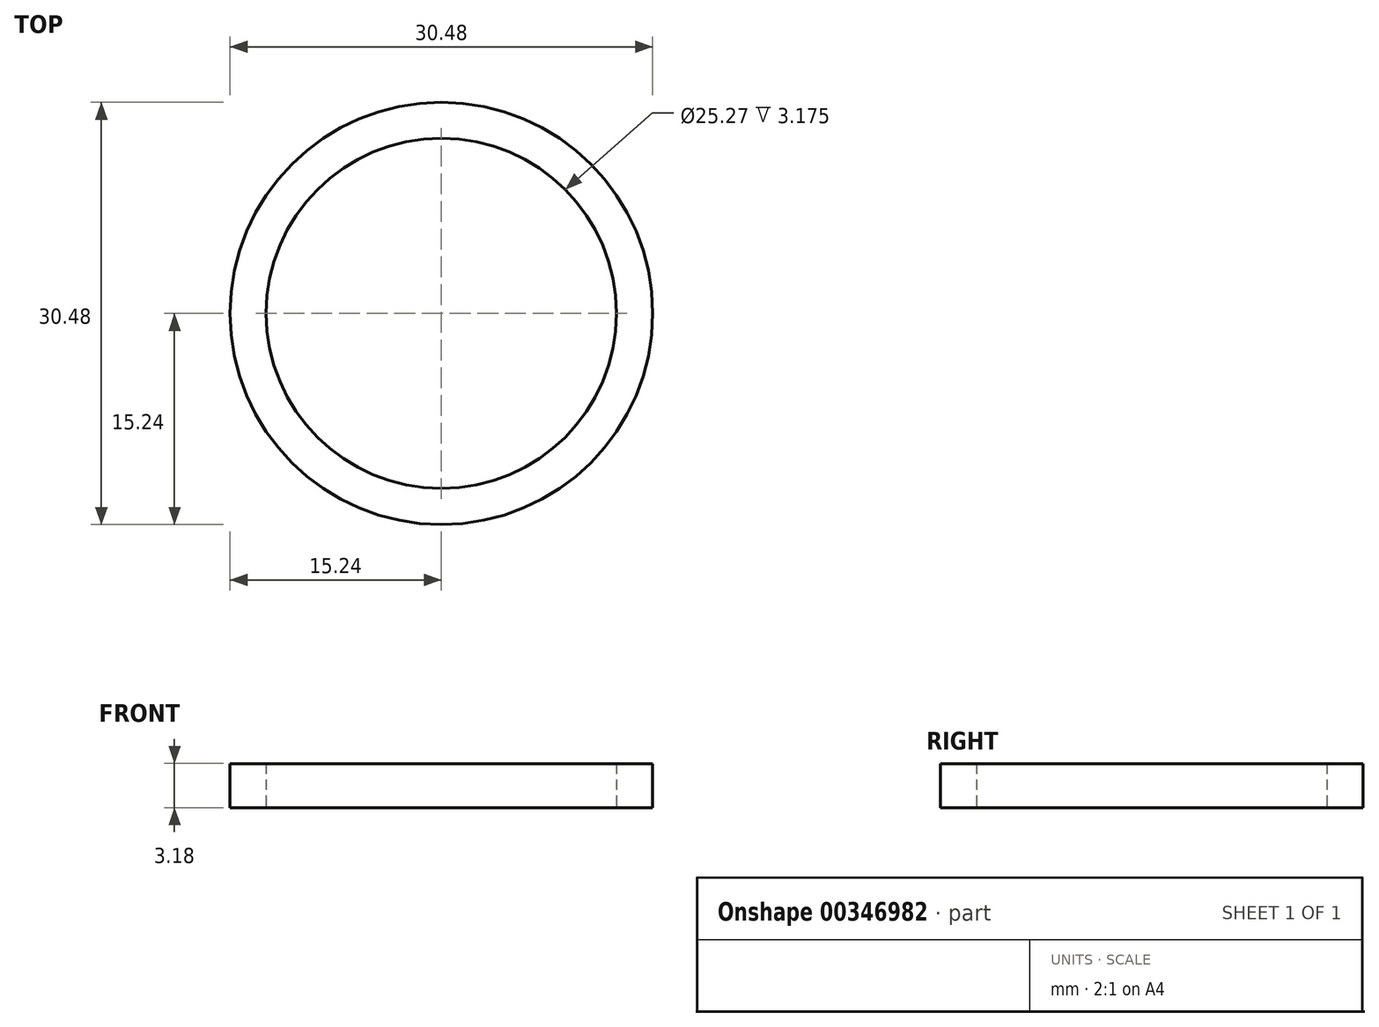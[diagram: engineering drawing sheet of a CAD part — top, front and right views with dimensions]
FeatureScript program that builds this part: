
annotation { "Feature Type Name" : "Feature", "Feature Type Description" : "" }
export const myFeature = defineFeature(function(context is Context, id is Id, definition is map)
    precondition{}
    {
        {
            var Q0;
            Q0=qCreatedBy(makeId("Top.planeOp"),FACE);
            var sketch = newSketch(context, id + "F0", { "sketchPlane" : qUnion([Q0])});
            skCircle(sketch, "E0", {"center": v(0, 0) * mm, "radius": 12.64 * mm});
            skCircle(sketch, "E1", {"center": v(0, 0) * mm, "radius": 15.24 * mm});
            skSolve(sketch);
        }
        {
            var Q0;
            Q0 = qSketchRegion(id + "F0", true);
            extrude(context, id + "F1", {"entities" : qUnion([Q0]), "depth" : 3.17 * mm});
        }
    });
